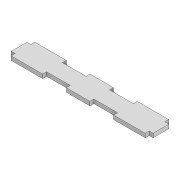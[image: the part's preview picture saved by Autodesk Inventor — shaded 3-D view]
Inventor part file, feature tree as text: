
AUTODESK INVENTOR PART (.ipt)
format: ipt  version: 2022 (Build 260153000, 153)  size: 117,760 bytes
history: native  units: mm
features: extrude x1, sketch x1
ambient origin geometry x8: Origin, YZ Plane, XZ Plane, XY Plane, X Axis, Y Axis, Z Axis, Center Point
bodies: Solid1 (feature_tree)
feature tree (2):
  extrude  "Extrusion1"  Depth=30.0mm
  sketch  "Sketch1"  dims[d0=170.0mm d1=30.0mm d2=5.0mm d3=20.0mm d4=5.0mm d5=5.0mm d6=20.0mm d7=5.0mm d8=5.0mm d9=0.0mm d17=30.0mm d18=5.0mm d19=30.0mm d20=30.0mm d21=15.0mm]
